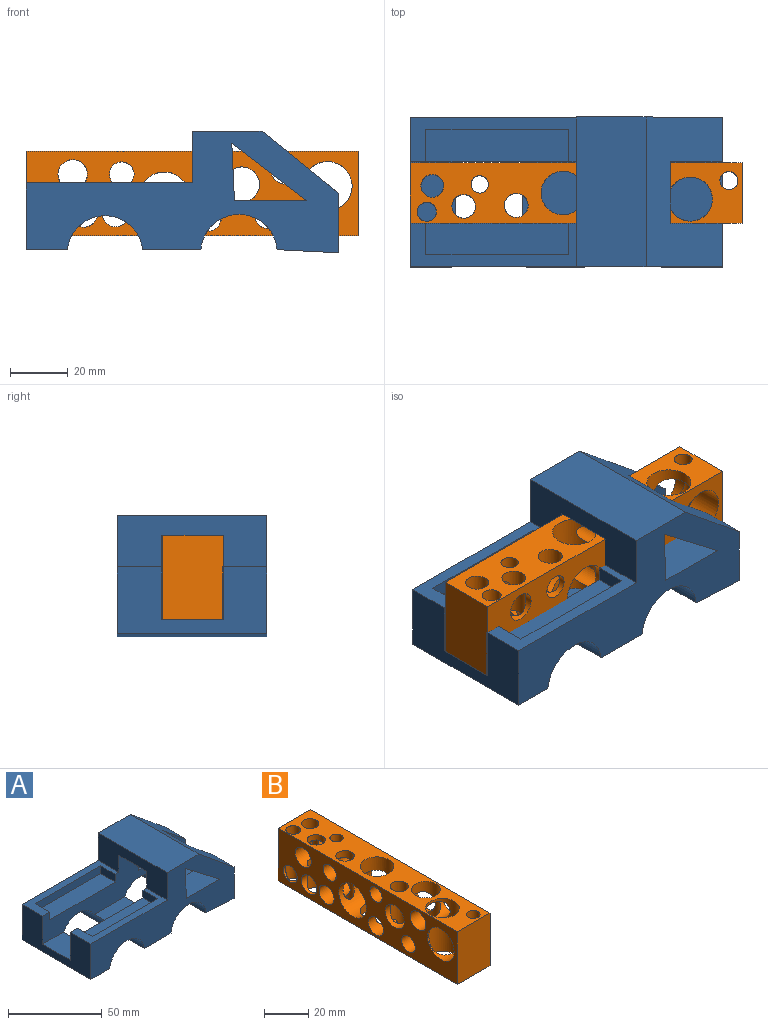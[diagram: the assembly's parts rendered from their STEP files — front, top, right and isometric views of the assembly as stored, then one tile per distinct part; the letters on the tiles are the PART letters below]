
ASSEMBLY  parts=2 mates=4
PART A: 33 faces, bbox 108x51.8x42.1 mm
  f0: plane 57.57x15.47mm, normal (0,0,1), area 342.4mm2, adj f1,f6,f7,f8,f18,f20,f31
  f1: plane 51.82x23.09mm, normal (-1,0,0), area 816.5mm2, adj f0,f13,f14,f18,f19,f26,f31,f32
  f2: cylinder r=13.12mm len=51.82mm, axis (0,1,0), area 1405.3mm2, adj f14,f15,f18,f19,f26,f27,f31,f32
  f3: cylinder r=13.21mm len=51.82mm, axis (0,1,0), area 1434.9mm2, adj f15,f16,f18,f19,f27,f28,f31,f32
  f4: plane 51.82x20.59mm, normal (1,0,0), area 761.3mm2, adj f5,f16,f18,f19,f28,f31,f32
  f5: plane 51.82x26.34mm, normal (0.63,0,0.78), area 1277.5mm2, adj f4,f17,f18,f19,f29,f31,f32
  f6: plane 51.82x17.89mm, normal (-1,0,0), area 696.3mm2, adj f0,f13,f17,f18,f19,f30,f31,f32
  f7: plane 11.1x5.08mm, normal (-1,0,0), area 56.4mm2, adj f0,f9,f20,f31
  f8: plane 11.1x5.08mm, normal (1,0,0), area 56.4mm2, adj f0,f9,f20,f31
  f9: plane 49.36x11.1mm, normal (0,0,1), area 548mm2, adj f7,f8,f20,f31
  f10: plane 51.82x25.95mm, normal (-0.61,0,-0.79), area 1107.2mm2, adj f11,f12,f18,f19,f25,f29,f31,f32
  f11: plane 51.82x19.95mm, normal (1,0,0.05), area 675.6mm2, adj f10,f12,f18,f19,f25,f30,f31,f32
  f12: plane 25.03x15.47mm, normal (0,0,1), area 387.2mm2, adj f10,f11,f18,f31
  f13: plane 57.57x15.47mm, normal (0,0,1), area 342.4mm2, adj f1,f6,f19,f21,f22,f23,f32
  f14: plane 51.82x14.27mm, normal (0,0,-1), area 739.5mm2, adj f1,f2,f18,f19
  f15: plane 51.82x20.13mm, normal (0,0,-1), area 1042.9mm2, adj f2,f3,f18,f19
  f16: plane 51.82x21.14mm, normal (-0.05,0,-1), area 1096.8mm2, adj f3,f4,f18,f19
  f17: plane 51.82x24.07mm, normal (0,0,1), area 1247.1mm2, adj f5,f6,f18,f19
  f18: plane 107.98x42.05mm, normal (0,-1,0), area 2392.2mm2, adj f0,f1,f2,f3,f4,f5,f6,f10
  f19: plane 107.98x42.05mm, normal (0,1,0), area 2392.2mm2, adj f1,f2,f3,f4,f5,f6,f10,f11
  f20: plane 49.36x5.08mm, normal (0,1,0), area 250.8mm2, adj f0,f7,f8,f9
  f21: plane 11.1x5.08mm, normal (-1,0,0), area 56.4mm2, adj f13,f22,f24,f32
  f22: plane 49.36x5.08mm, normal (0,-1,0), area 250.8mm2, adj f13,f21,f23,f24
  f23: plane 11.1x5.08mm, normal (1,0,0), area 56.4mm2, adj f13,f22,f24,f32
  f24: plane 49.36x11.1mm, normal (0,0,1), area 548mm2, adj f21,f22,f23,f32
  f25: plane 25.03x15.47mm, normal (0,0,1), area 387.2mm2, adj f10,f11,f19,f32
  f26: plane 20.88x15.79mm, normal (0,0,1), area 329.8mm2, adj f1,f2,f31,f32
  f27: plane 23x20.88mm, normal (0,0,1), area 480.3mm2, adj f2,f3,f31,f32
  f28: plane 22.49x20.88mm, normal (0,0,1), area 469.7mm2, adj f3,f4,f31,f32
  f29: plane 20.88x15.26mm, normal (0,0,-1), area 318.6mm2, adj f5,f10,f31,f32
  f30: plane 20.88x13.74mm, normal (0,0,-1), area 286.9mm2, adj f6,f11,f31,f32
  f31: plane 107.98x29.24mm, normal (0,1,0), area 1659mm2, adj f0,f1,f2,f3,f4,f5,f6,f7
  f32: plane 107.98x29.24mm, normal (0,-1,0), area 1659mm2, adj f1,f2,f3,f4,f5,f6,f10,f11
PART B: 30 faces, bbox 20.9x114.8x29.2 mm
  f0: cylinder r=4.33mm len=12.45mm, axis (1,0,0), area 225.5mm2, adj f3,f24
  f1: plane 114.83x29.24mm, normal (1,0,0), area 2156.5mm2, adj f2,f4,f5,f6,f7,f8,f9,f10
  f2: plane 29.24x20.88mm, normal (0,1,0), area 610.4mm2, adj f1,f3,f5,f6
  f3: plane 114.83x29.24mm, normal (-1,0,0), area 2156.5mm2, adj f0,f2,f4,f5,f6,f7,f8,f9
  f4: plane 29.24x20.88mm, normal (0,-1,0), area 610.4mm2, adj f1,f3,f5,f6
  f5: plane 114.83x20.88mm, normal (0,0,1), area 1599mm2, adj f1,f2,f3,f4,f19,f20,f21,f22
  f6: plane 114.83x20.88mm, normal (0,0,-1), area 1599mm2, adj f1,f2,f3,f4,f19,f20,f21,f22
  f7: cylinder r=4.99mm len=20.88mm, axis (1,0,0), area 449.6mm2, adj f1,f3,f22,f29
  f8: cylinder r=5.09mm len=20.88mm, axis (1,0,0), area 514.8mm2, adj f1,f3,f22,f27,f29
  f9: cylinder r=4.41mm len=20.88mm, axis (1,0,0), area 375.3mm2, adj f1,f3,f26,f27,f28
  f10: cylinder r=5.01mm len=20.88mm, axis (1,0,0), area 354.5mm2, adj f1,f3,f19,f24
  f11: cylinder r=6.09mm len=20.88mm, axis (1,0,0), area 452.4mm2, adj f1,f3,f24,f25
  f12: cylinder r=4.84mm len=20.88mm, axis (1,0,0), area 518.8mm2, adj f1,f3,f23,f25
  f13: cylinder r=4.33mm len=8.67mm, axis (1,0,0), area 69.6mm2, adj f1,f24
  f14: cylinder r=3.92mm len=20.88mm, axis (1,0,0), area 455.1mm2, adj f1,f3,f23
  f15: cylinder r=8.83mm len=20.88mm, axis (1,0,0), area 661.6mm2, adj f1,f3,f21,f23
  f16: cylinder r=4.26mm len=20.88mm, axis (1,0,0), area 453.2mm2, adj f1,f3,f21
  f17: cylinder r=4.83mm len=20.88mm, axis (1,0,0), area 531.2mm2, adj f1,f3,f21,f22
  f18: cylinder r=8.52mm len=20.88mm, axis (1,0,0), area 650.4mm2, adj f1,f3,f19,f20
  f19: cylinder r=7.62mm len=29.24mm, axis (0,0,1), area 846.6mm2, adj f5,f6,f10,f18
  f20: cylinder r=3.1mm len=29.24mm, axis (0,0,1), area 378.6mm2, adj f5,f6,f18
  f21: cylinder r=4.15mm len=29.24mm, axis (0,0,1), area 497.3mm2, adj f5,f6,f15,f16,f17
  f22: cylinder r=3.01mm len=29.24mm, axis (0,0,1), area 441.1mm2, adj f5,f6,f7,f8,f17
  f23: cylinder r=7.6mm len=29.24mm, axis (0,0,1), area 765.8mm2, adj f5,f6,f12,f14,f15
  f24: cylinder r=6.49mm len=29.24mm, axis (0,0,1), area 743.4mm2, adj f0,f5,f6,f10,f11,f13
  f25: cylinder r=4.13mm len=29.24mm, axis (0,0,1), area 555.2mm2, adj f5,f6,f11,f12
  f26: cylinder r=3.32mm len=29.24mm, axis (0,0,1), area 493.5mm2, adj f5,f6,f9
  f27: cylinder r=3.94mm len=19.94mm, axis (0,0,1), area 430.7mm2, adj f5,f8,f9
  f28: cylinder r=3.94mm len=7.87mm, axis (0,0,1), area 112.6mm2, adj f6,f9
  f29: cylinder r=4.1mm len=29.24mm, axis (0,0,1), area 411.8mm2, adj f5,f6,f7,f8
PLACE A t=(42.38,10.59,-13.17)mm fixed
PLACE B rot(axis=(0,0,1),90deg) t=(51.5,10.23,-17.22)mm
MATE parallel B.f2 <-> A.f1  axis (-1,0,0) through (-5.92,10.23,-2.6)mm
MATE planar B.f5 <-> A.f29  axis (0,0,1) through (49.27,10.59,12.02)mm
MATE parallel B.f5 <-> A.f27  axis (0,0,1) through (49.27,10.59,12.02)mm
MATE planar B.f2 <-> A.f1  axis (-1,0,0) through (-5.92,10.23,-2.6)mm
